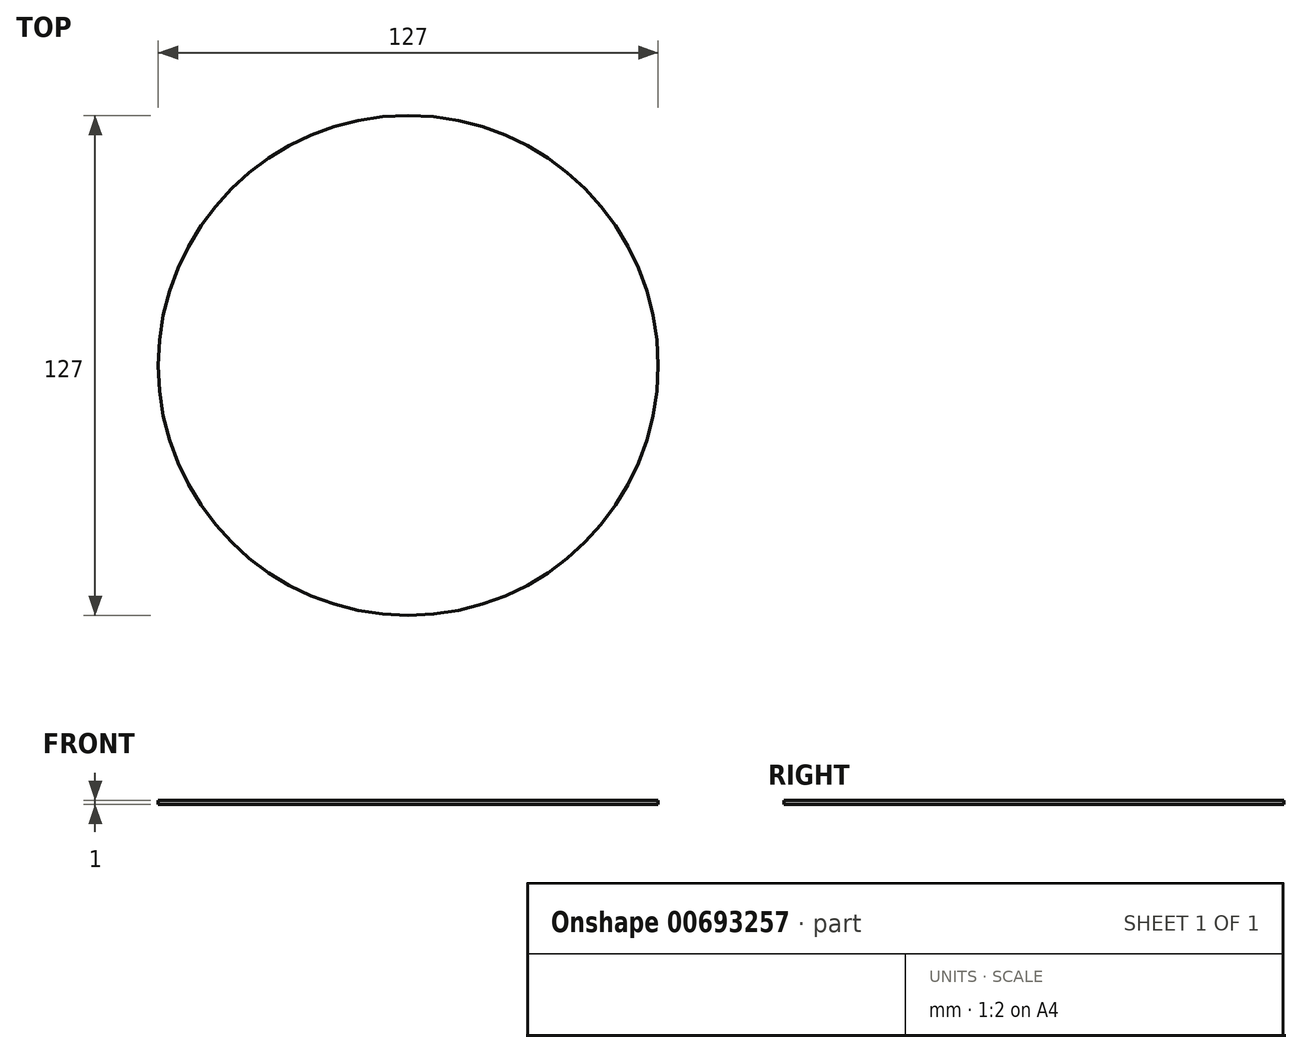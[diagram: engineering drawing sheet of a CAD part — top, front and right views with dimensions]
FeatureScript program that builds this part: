
annotation { "Feature Type Name" : "Feature", "Feature Type Description" : "" }
export const myFeature = defineFeature(function(context is Context, id is Id, definition is map)
    precondition{}
    {
        {
            var Q0;
            Q0=qCreatedBy(makeId("Top.planeOp"),FACE);
            var sketch = newSketch(context, id + "F0", { "sketchPlane" : qUnion([Q0])});
            skCircle(sketch, "E0", {"center": v(-3.26, 0) * mm, "radius": 63.5 * mm});
            skSolve(sketch);
        }
        {
            var Q0;
            Q0=makeQuery(id+"F0.imprint","IMPRINT",FACE,{"disambiguationData":[TD([[makeQuery(id+"F0.imprint","IMPRINT",EDGE,{"derivedFrom":sQuery(id+"F0.wireOp",EDGE,"E0")}),1.0]])]});
            extrude(context, id + "F1", {"entities" : qUnion([Q0]), "depth" : 1 * mm, "offsetDistance" : 25 * mm});
        }
    });
